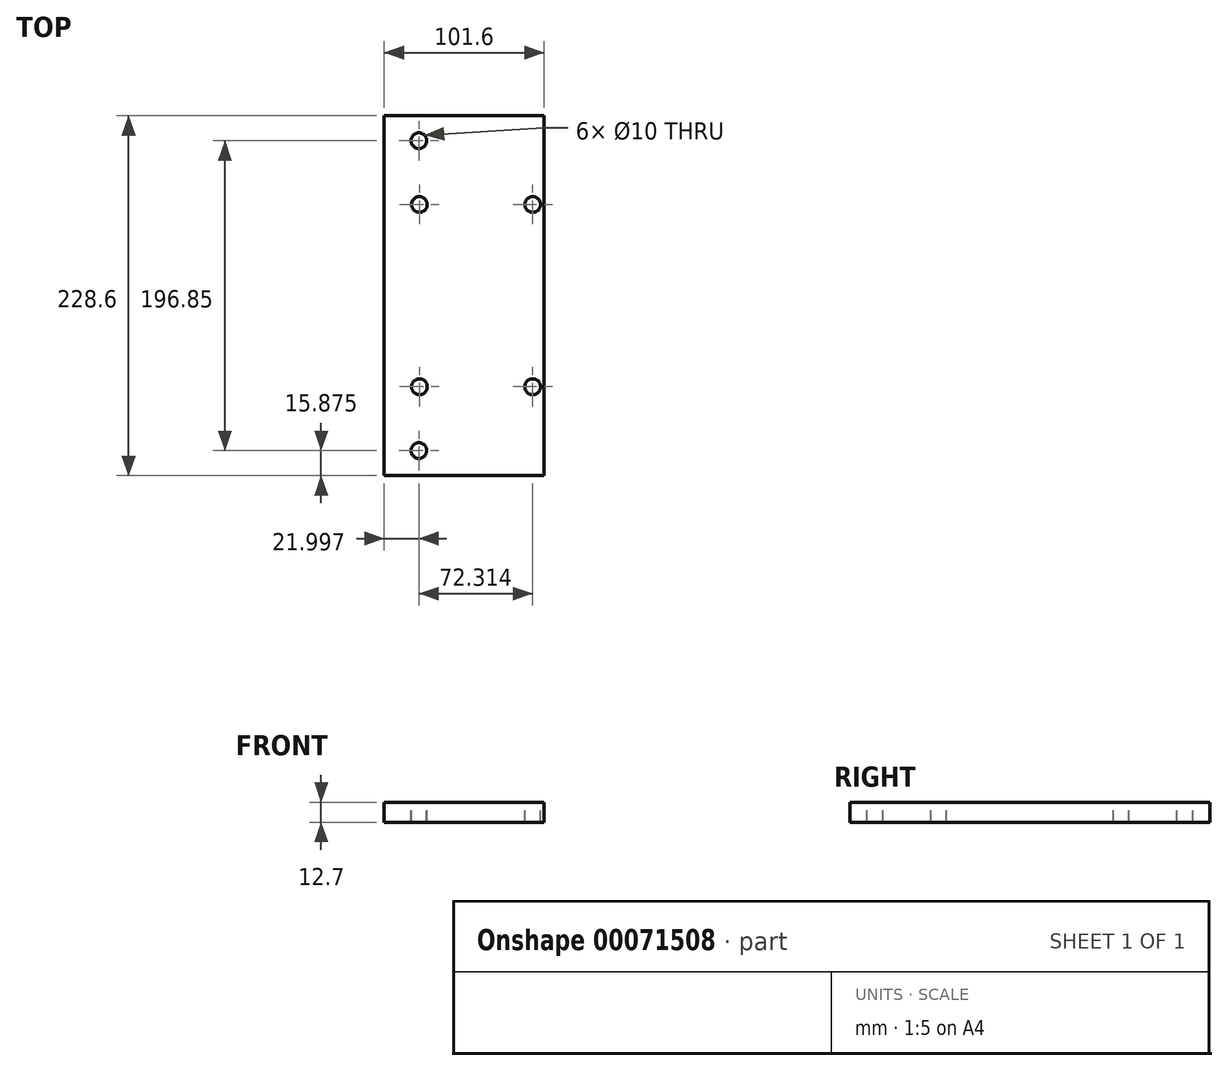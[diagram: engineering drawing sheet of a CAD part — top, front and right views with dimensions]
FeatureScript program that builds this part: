
annotation { "Feature Type Name" : "Feature", "Feature Type Description" : "" }
export const myFeature = defineFeature(function(context is Context, id is Id, definition is map)
    precondition{}
    {
        {
            var Q0;
            Q0=qCreatedBy(makeId("Front.planeOp"),FACE);
            var sketch = newSketch(context, id + "F0", { "sketchPlane" : qUnion([Q0])});
            skLineSegment(sketch, "E0.bottom", {"start": v(-59.95, 1.62) * mm, "end": v(41.65, 1.62) * mm});
            skLineSegment(sketch, "E0.top", {"start": v(-59.95, -11.08) * mm, "end": v(41.65, -11.08) * mm});
            skLineSegment(sketch, "E0.left", {"start": v(-59.95, 1.62) * mm, "end": v(-59.95, -11.08) * mm});
            skLineSegment(sketch, "E0.right", {"start": v(41.65, 1.62) * mm, "end": v(41.65, -11.08) * mm});
            skSolve(sketch);
        }
        {
            var Q0;
            Q0 = qSketchRegion(id + "F0", true);
            extrude(context, id + "F1", {"entities" : qUnion([Q0]), "depth" : 228.6 * mm});
        }
        {
            var Q0;
            Q0=makeQuery(id+"F1.opExtrude","SWEPT_FACE",FACE,{"disambiguationData":[OSD([sQuery(id+"F0.wireOp",EDGE,"E0.bottom")])]});
            var sketch = newSketch(context, id + "F2", { "sketchPlane" : qUnion([Q0])});
            skCircle(sketch, "E1", {"center": v(34.36, -56.4) * mm, "radius": 5 * mm});
            skCircle(sketch, "E2.0.1.0", {"center": v(34.36, -172.2) * mm, "radius": 5 * mm});
            skCircle(sketch, "E2.1.0.0", {"center": v(-37.64, -56.4) * mm, "radius": 5 * mm});
            skCircle(sketch, "E2.1.1.0", {"center": v(-37.64, -172.2) * mm, "radius": 5 * mm});
            skLineSegment(sketch, "E2.direction1", {"start": v(34.36, -56.4) * mm, "end": v(-37.64, -56.4) * mm, "construction": true});
            skLineSegment(sketch, "E2.direction2", {"start": v(34.36, -56.4) * mm, "end": v(34.36, -172.2) * mm, "construction": true});
            skCircle(sketch, "E3", {"center": v(-37.95, -212.73) * mm, "radius": 5 * mm});
            skCircle(sketch, "E4.0.1.0", {"center": v(-37.95, -15.88) * mm, "radius": 5 * mm});
            skLineSegment(sketch, "E4.direction1", {"start": v(-37.95, -212.73) * mm, "end": v(34.05, -212.73) * mm, "construction": true});
            skLineSegment(sketch, "E4.direction2", {"start": v(-37.95, -212.73) * mm, "end": v(-37.95, -15.88) * mm, "construction": true});
            skSolve(sketch);
        }
        {
            var Q0;
            Q0 = qSketchRegion(id + "F2", true);
            extrude(context, id + "F3", {"entities" : qUnion([Q0]), "operationType" : NewBodyOperationType.REMOVE, "endBound" : BoundingType.THROUGH_ALL, "oppositeDirection" : true, "depth" : 25 * mm});
        }
    });
